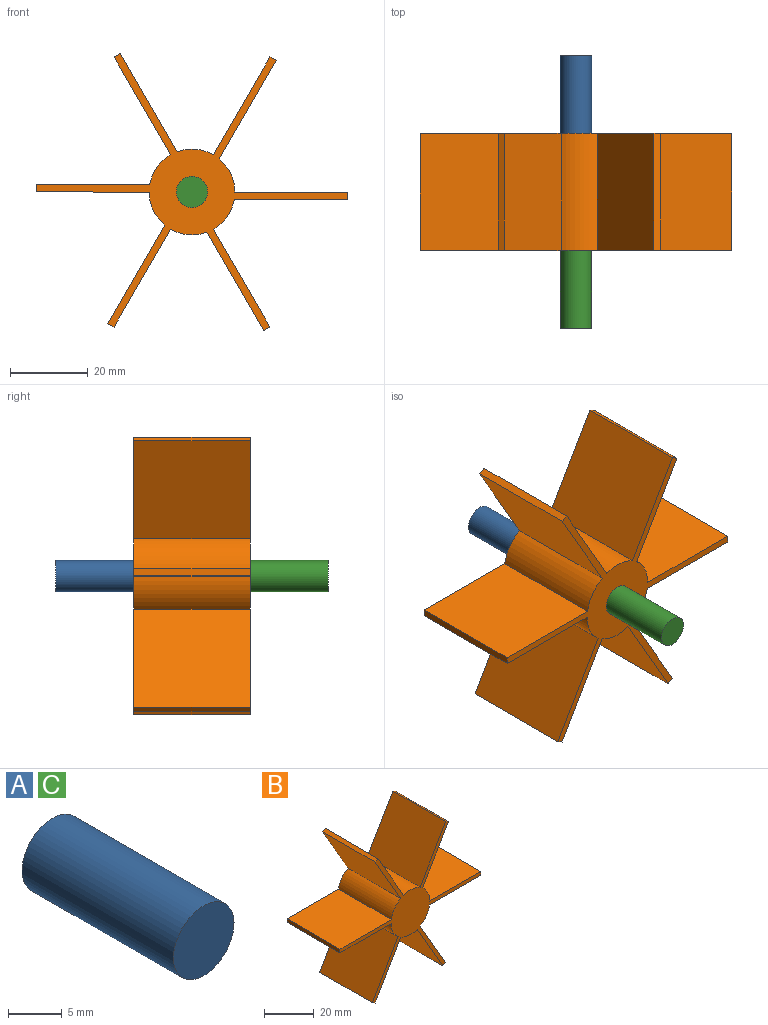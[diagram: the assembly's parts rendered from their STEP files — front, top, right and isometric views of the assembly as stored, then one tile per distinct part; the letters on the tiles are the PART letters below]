
ASSEMBLY  parts=3 mates=2
PART A: 3 faces, bbox 8x20x8 mm
  f0: cylinder r=4mm len=20mm, axis (0,1,0), area 502.7mm2, adj f1,f2
  f1: plane 8x8mm, normal (0,-1,0), area 50.3mm2, adj f0
  f2: plane 8x8mm, normal (0,1,0), area 50.3mm2, adj f0
PART B: 28 faces, bbox 80x30x71.1 mm
  f0: cylinder r=11mm len=30mm, axis (0,1,0), area 290.3mm2, adj f1,f23,f24,f25
  f1: plane 30x25.25mm, normal (-0.87,0,0.5), area 874.6mm2, adj f0,f2,f24,f25
  f2: plane 30x1.59mm, normal (-0.5,0,-0.87), area 55mm2, adj f1,f3,f24,f25
  f3: plane 30x25.11mm, normal (0.87,0,-0.5), area 870mm2, adj f2,f4,f24,f25
  f4: cylinder r=11mm len=30mm, axis (0,1,0), area 290.3mm2, adj f3,f5,f24,f25
  f5: plane 30x25.25mm, normal (-0.87,0,-0.5), area 874.6mm2, adj f4,f6,f24,f25
  f6: plane 30x1.59mm, normal (0.5,0,-0.87), area 55mm2, adj f5,f7,f24,f25
  f7: plane 30x25.11mm, normal (0.87,0,0.5), area 870mm2, adj f6,f8,f24,f25
  f8: cylinder r=11mm len=30mm, axis (0,1,0), area 290.3mm2, adj f7,f9,f24,f25
  f9: plane 30x29.15mm, normal (0,0,-1), area 874.6mm2, adj f8,f10,f24,f25
  f10: plane 30x1.83mm, normal (1,0,0), area 55mm2, adj f9,f11,f24,f25
  f11: plane 30x29mm, normal (0,0,1), area 870mm2, adj f10,f12,f24,f25
  f12: cylinder r=11mm len=30mm, axis (0,1,0), area 290.3mm2, adj f11,f13,f24,f25
  f13: plane 30x25.25mm, normal (0.87,0,-0.5), area 874.6mm2, adj f12,f14,f24,f25
  f14: plane 30x1.59mm, normal (0.5,0,0.87), area 55mm2, adj f13,f15,f24,f25
  f15: plane 30x25.11mm, normal (-0.87,0,0.5), area 870mm2, adj f14,f16,f24,f25
  f16: cylinder r=11mm len=30mm, axis (0,1,0), area 290.3mm2, adj f15,f17,f24,f25
  f17: plane 30x25.25mm, normal (0.87,0,0.5), area 874.6mm2, adj f16,f18,f24,f25
  f18: plane 30x1.59mm, normal (-0.5,0,0.87), area 55mm2, adj f17,f19,f24,f25
  f19: plane 30x25.11mm, normal (-0.87,0,-0.5), area 870mm2, adj f18,f20,f24,f25
  f20: cylinder r=11mm len=30mm, axis (0,1,0), area 290.3mm2, adj f19,f21,f24,f25
  f21: plane 30x29.15mm, normal (0,0,1), area 874.6mm2, adj f20,f22,f24,f25
  f22: plane 30x1.83mm, normal (-1,0,0), area 55mm2, adj f21,f23,f24,f25
  f23: plane 30x29mm, normal (0,0,-1), area 870mm2, adj f0,f22,f24,f25
  f24: plane 80x71.12mm, normal (0,-1,0), area 699.8mm2, adj f0,f1,f2,f3,f4,f5,f6,f7
  f25: plane 80x71.12mm, normal (0,1,0), area 650.8mm2, adj f0,f1,f2,f3,f4,f5,f6,f7
  f26: cylinder r=3.95mm len=10mm, axis (0,1,0), area 248.2mm2, adj f25,f27
  f27: plane 7.9x7.9mm, normal (0,1,0), area 49mm2, adj f26
PART C: same geometry as A
PLACE A rot(axis=(1,0,0),180deg) t=(-0.07,15.17,0.32)mm
PLACE B t=(-0.07,15.17,0.32)mm
PLACE C t=(-0.07,-14.83,0.32)mm
MATE fastened C.f0 <-> B.f0  axis (0,1,0) through (-0.07,-14.83,0.32)mm
MATE fastened A.f0 <-> B.f4  axis (0,-1,0) through (-0.07,15.17,0.32)mm
